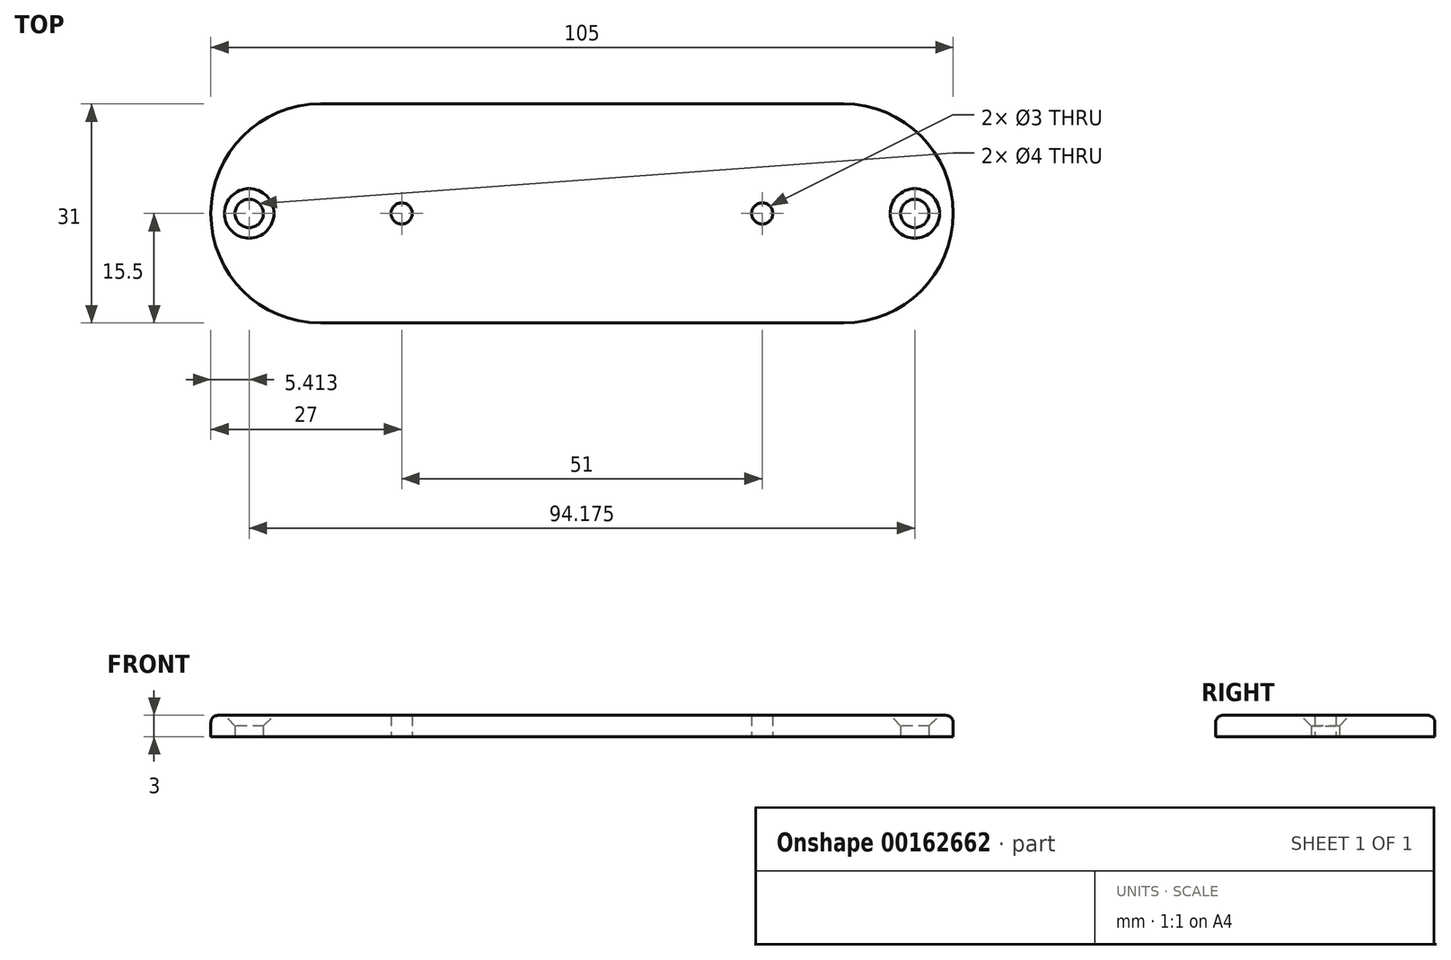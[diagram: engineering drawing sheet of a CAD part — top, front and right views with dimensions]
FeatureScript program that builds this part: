
annotation { "Feature Type Name" : "Feature", "Feature Type Description" : "" }
export const myFeature = defineFeature(function(context is Context, id is Id, definition is map)
    precondition{}
    {
        {
            var Q0;
            Q0=qCreatedBy(makeId("Top.planeOp"),FACE);
            var sketch = newSketch(context, id + "F0", { "sketchPlane" : qUnion([Q0])});
            skLineSegment(sketch, "E0.bottom", {"start": v(-37, 15.5) * mm, "end": v(37, 15.5) * mm});
            skLineSegment(sketch, "E0.top", {"start": v(-37, -15.5) * mm, "end": v(37, -15.5) * mm});
            skPoint(sketch, "E0.middle", {"position": v(0, 0) * mm});
            skArc(sketch, "E1", {"start": v(-37, 15.5) * mm, "mid": v(-52.5, 0) * mm, "end": v(-37, -15.5) * mm});
            skArc(sketch, "E2", {"start": v(37, -15.5) * mm, "mid": v(52.5, 0) * mm, "end": v(37, 15.5) * mm});
            skCircle(sketch, "E3", {"center": v(-25.5, 0) * mm, "radius": 1.5 * mm});
            skCircle(sketch, "E4", {"center": v(25.5, 0) * mm, "radius": 1.5 * mm});
            skCircle(sketch, "E5", {"center": v(-47.09, 0) * mm, "radius": 2 * mm});
            skCircle(sketch, "E6.MirrorC", {"center": v(47.09, 0) * mm, "radius": 2 * mm});
            skSolve(sketch);
        }
        {
            var Q0;
            Q0 = qSketchRegion(id + "F0", true);
            extrude(context, id + "F1", {"entities" : qUnion([Q0]), "depth" : 3 * mm, "offsetDistance" : 25 * mm});
        }
        {
            var Q0;
            Q0=makeQuery(id+"F1.opExtrude","CAP_EDGE",EDGE,{"disambiguationData":[OSD([sQuery(id+"F0.wireOp",EDGE,"E1")])],"isStart":false});
            fillet(context, id + "F2", {"entities" : qUnion([Q0]), "radius" : 1 * mm, "tangentPropagation" : true, "allowEdgeOverflow" : false});
        }
        {
            var Q0;
            Q0=makeQuery(id+"F1.opExtrude","CAP_EDGE",EDGE,{"disambiguationData":[OSD([sQuery(id+"F0.wireOp",EDGE,"E5")])],"isStart":false});
            var Q1;
            Q1=makeQuery(id+"F1.opExtrude","CAP_EDGE",EDGE,{"disambiguationData":[OSD([sQuery(id+"F0.wireOp",EDGE,"E6.MirrorC")])],"isStart":false});
            chamfer(context, id + "F3", {"entities" : qUnion([Q0, Q1]), "width" : 1.5 * mm, "tangentPropagation" : true});
        }
    });
